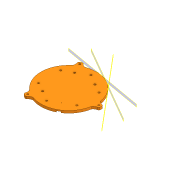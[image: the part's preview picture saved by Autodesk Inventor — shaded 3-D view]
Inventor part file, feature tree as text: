
AUTODESK INVENTOR PART (.ipt)
format: ipt  version: 2020.3 (Build 243373000, 373)  size: 299,008 bytes
history: native  units: mm
features: extrude x8, sketch x4, plane x3, fillet x2, pattern_circular x1
ambient origin geometry x8: Origin, YZ Plane, XZ Plane, XY Plane, X Axis, Y Axis, Z Axis, Center Point
bodies: Solid1 (feature_tree)
feature tree (18):
  sketch  "Sketch1"  dims[d0=95.0mm d1=120.0deg]
  extrude  "Extrusion1"  TaperAngle=120.0deg  [1 undecoded]
  plane  "Work Plane1"
  plane  "Work Plane2"
  plane  "Work Plane3"
  extrude  "Extrusion2"  Depth=16.0mm
  extrude  "Extrusion3"  Depth=6.0mm
  sketch  "Sketch2"  dims[d2=120.0deg d3=16.0mm]
  sketch  "Sketch3"  dims[d4=3.0mm d5=6.0mm]
  extrude  "Extrusion4"  Depth=10.0mm
  extrude  "Extrusion5"  Depth=10.0mm
  extrude  "Extrusion6"  Depth=10.0mm
  fillet  "Fillet1"  Radius=1.2mm
  fillet  "Fillet2"  Radius=4.0mm
  extrude  "Extrusion7"  Depth=10.0mm TaperAngle=360.0deg
  pattern_circular  "Circular Pattern1"  [2 undecoded]
  extrude  "Extrusion8"  Depth=10.0mm
  sketch  "Sketch4"  dims[d6=1.0mm d7=10.0mm d8=3.6mm d9=2.4mm d10=1.2mm d11=4.0mm d12=0.0mm d13=30.0mm d15=360.0deg d17=9.6mm d18=12.0mm d19=2.0mm d20=6.0mm d21=2.0mm d23=60.0deg d24=6.1mm d25=8.0mm d26=6.1mm d27=60.0deg d28=3.490659mm d29=3.490659mm d39=90.0deg d40=90.0deg d41=90.0deg d42=5.0mm d43=0.0mm d44=2.0mm d45=0.0mm d46=5.5mm d47=5.5mm d48=5.5mm d49=24.0mm d50=0.0mm d51=24.0mm d52=0.0mm d53=24.0mm d54=0.0mm d55=6.0mm d56=40.0mm d57=60.0mm d58=3.2mm d59=1.0mm d60=1.0mm d61=1.0mm d62=1.0mm d63=6.0mm d64=3.0mm d65=8.0mm d66=6.0mm d67=10.0mm d68=0.0mm d69=60.0mm d70=360.0deg d72=10.0mm d73=0.0mm d74=0.5mm d75=0.872665mm d76=0.5mm d77=0.872665mm]
note: 3 required parameter values undecoded (feature->parameter linkage not recoverable at this tier; creation-order binding heuristic only, values carry confidence <= 0.55)
